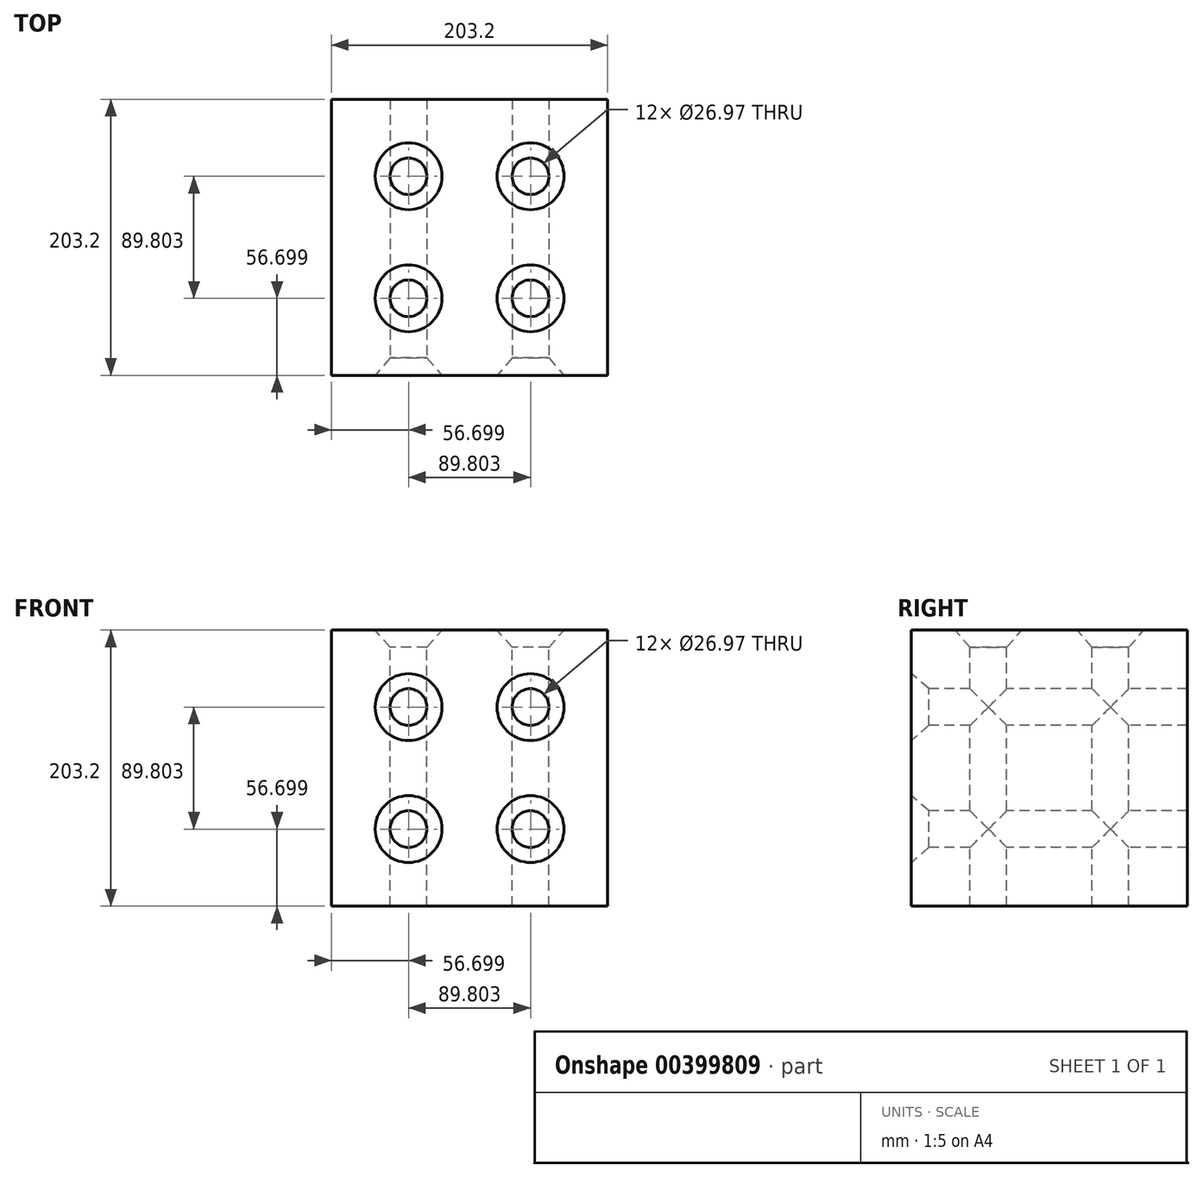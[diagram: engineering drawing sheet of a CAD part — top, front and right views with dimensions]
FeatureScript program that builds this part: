
annotation { "Feature Type Name" : "Feature", "Feature Type Description" : "" }
export const myFeature = defineFeature(function(context is Context, id is Id, definition is map)
    precondition{}
    {
        {
            var Q0;
            Q0=qCreatedBy(makeId("Front.planeOp"),FACE);
            var sketch = newSketch(context, id + "F0", { "sketchPlane" : qUnion([Q0])});
            skLineSegment(sketch, "E0.bottom", {"start": v(0, 0) * mm, "end": v(-203.2, 0) * mm});
            skLineSegment(sketch, "E0.top", {"start": v(0, 203.2) * mm, "end": v(-203.2, 203.2) * mm});
            skLineSegment(sketch, "E0.left", {"start": v(0, 0) * mm, "end": v(0, 203.2) * mm});
            skLineSegment(sketch, "E0.right", {"start": v(-203.2, 0) * mm, "end": v(-203.2, 203.2) * mm});
            skSolve(sketch);
        }
        {
            var Q0;
            Q0 = qSketchRegion(id + "F0", true);
            extrude(context, id + "F1", {"entities" : qUnion([Q0]), "endBound" : BoundingType.SYMMETRIC, "depth" : 203.2 * mm});
        }
        {
            var Q0;
            Q0=makeQuery(id+"F1.opExtrude","CAP_FACE",FACE,{"disambiguationData":[OSD([sQuery(id+"F0.wireOp",EDGE,"E0.bottom"),sQuery(id+"F0.wireOp",EDGE,"E0.top"),sQuery(id+"F0.wireOp",EDGE,"E0.left"),sQuery(id+"F0.wireOp",EDGE,"E0.right")])],"isStart":false});
            var sketch = newSketch(context, id + "F2", { "sketchPlane" : qUnion([Q0])});
            skPoint(sketch, "E1.centerSnap0", {"position": v(-101.6, 0) * mm});
            skLineSegment(sketch, "E2", {"start": v(-203.2, 203.2) * mm, "end": v(0, 0) * mm});
            skLineSegment(sketch, "E3", {"start": v(0, 203.2) * mm, "end": v(-203.2, 0) * mm});
            skCircle(sketch, "E4", {"center": v(-101.6, 101.6) * mm, "radius": 63.5 * mm});
            skPoint(sketch, "E5", {"position": v(-146.5, 146.5) * mm});
            skPoint(sketch, "E6", {"position": v(-146.5, 56.7) * mm});
            skPoint(sketch, "E7", {"position": v(-56.7, 146.5) * mm});
            skPoint(sketch, "E8", {"position": v(-56.7, 56.7) * mm});
            skSolve(sketch);
        }
        {
            var Q0;
            Q0=sQuery(id+"F2.wireOp",VERTEX,"E7");
            var Q1;
            Q1=sQuery(id+"F2.wireOp",VERTEX,"E5");
            var Q2;
            Q2=sQuery(id+"F2.wireOp",VERTEX,"E6");
            var Q3;
            Q3=sQuery(id+"F2.wireOp",VERTEX,"E8");
            var Q4;
            Q4=makeQuery(id+"F1.opExtrude","SWEPT_BODY",BODY,{"disambiguationData":[OSD([sQuery(id+"F0.wireOp",EDGE,"E0.bottom"),sQuery(id+"F0.wireOp",EDGE,"E0.top"),sQuery(id+"F0.wireOp",EDGE,"E0.left"),sQuery(id+"F0.wireOp",EDGE,"E0.right")])]});
            hole(context, id + "F3", {"style" : HoleStyle.C_SINK, "endStyle" : HoleEndStyle.THROUGH, "holeDiameter" : 26.97 * mm, "cSinkDiameter" : 49.23 * mm, "cSinkAngle" : 82 * degree, "isTappedThrough" : true, "tappedDepth" : 12.7 * mm, "tapClearance" : 3, "locations" : qUnion([Q0, Q1, Q2, Q3]), "scope" : qUnion([Q4])});
        }
        {
            var Q0;
            Q0=makeQuery(id+"F1.opExtrude","SWEPT_FACE",FACE,{"disambiguationData":[OSD([sQuery(id+"F0.wireOp",EDGE,"E0.top")])]});
            var sketch = newSketch(context, id + "F4", { "sketchPlane" : qUnion([Q0])});
            skLineSegment(sketch, "E9", {"start": v(-203.2, 101.6) * mm, "end": v(0, -101.6) * mm});
            skLineSegment(sketch, "E10", {"start": v(-203.2, -101.6) * mm, "end": v(0, 101.6) * mm});
            skCircle(sketch, "E11", {"center": v(-101.6, 0) * mm, "radius": 63.5 * mm});
            skPoint(sketch, "E12", {"position": v(-146.5, 44.9) * mm});
            skPoint(sketch, "E13", {"position": v(-56.7, 44.9) * mm});
            skPoint(sketch, "E14", {"position": v(-56.7, -44.9) * mm});
            skPoint(sketch, "E15", {"position": v(-146.5, -44.9) * mm});
            skSolve(sketch);
        }
        {
            var Q0;
            Q0=sQuery(id+"F4.wireOp",VERTEX,"E13");
            var Q1;
            Q1=sQuery(id+"F4.wireOp",VERTEX,"E12");
            var Q2;
            Q2=sQuery(id+"F4.wireOp",VERTEX,"E15");
            var Q3;
            Q3=sQuery(id+"F4.wireOp",VERTEX,"E14");
            var Q4;
            Q4=makeQuery(id+"F1.opExtrude","SWEPT_BODY",BODY,{"disambiguationData":[OSD([sQuery(id+"F0.wireOp",EDGE,"E0.bottom"),sQuery(id+"F0.wireOp",EDGE,"E0.top"),sQuery(id+"F0.wireOp",EDGE,"E0.left"),sQuery(id+"F0.wireOp",EDGE,"E0.right")])]});
            hole(context, id + "F5", {"style" : HoleStyle.C_SINK, "endStyle" : HoleEndStyle.THROUGH, "holeDiameter" : 26.97 * mm, "cSinkDiameter" : 49.23 * mm, "cSinkAngle" : 82 * degree, "isTappedThrough" : true, "tappedDepth" : 12.7 * mm, "tapClearance" : 3, "locations" : qUnion([Q0, Q1, Q2, Q3]), "scope" : qUnion([Q4])});
        }
    });
